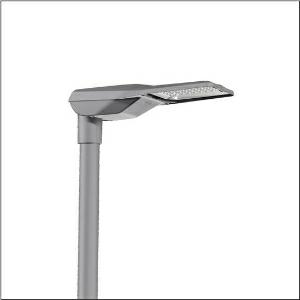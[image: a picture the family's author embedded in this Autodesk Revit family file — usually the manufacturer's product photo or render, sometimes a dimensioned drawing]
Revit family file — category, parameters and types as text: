
# Revit family: streetlight_sl_21_iq_mini___st0_8a_5xe2c21d08hb_7297
name_source: partatom
category: Lighting Fixtures
units: mm (PartAtom-declared; Revit-internal decimal feet)

## family parameters
Cut with Voids When Loaded = No
Host = Face
Light Source = No
Part Type = Normal
Room Calculation Point = No
Round Connector Dimension = Use Diameter
Shared = No

## types (1)
- --- (1 x LED, 7830 lm, 70.9 W, 2200K)
    Apparent Load = 71 VA
    CIE Flux Codes = 38 75 97 100 100
    Color Rendering = 70
    Color Temperature = 2200K
    Default Elevation = 1800 mm
    Description = Streetlight SL 21 iQ mini, mast luminaire, primary light control with lens, of PMMA, primary optical cover: cover, of toughened safety glass, transparent, light distribution: ST0.8a, light emission: direct distribution, primary light characteristic: asymmetric, installation type: post-top, side-entry, LED, High Power LED, rated luminous flux: 7.830lm, luminous efficacy: 110lm/W, light colour: 722, colour temperature: 2200K, control gear: iQ-Comfort, control: Auto-Match, Temp-Guard, Lumen-Switch, Night-Set, Smart-Wire, Light-Fading, Desk-Remote (wireless, voltage-free reading and setting of iQ features in the workshop via application-optimized NFC function/RFID function), optimised constant luminous flux control (CLO 2.0), pre-setting: linear dimming characteristic, mains connection: 220..240V, AC, 50/60Hz, start of lifetime: 71W, end of service life: 75W, reduction: 31W, luminaire housing, of diecast aluminium, powder-coated, Siteco® metallic grey (DB 702S), corrosivity category C5 mid according to DIN EN ISO 12944, please order mast flange separately, inclination adjustable: 0°, 5°, 10°, 15°, sealing non-destructively replaceable, multi-level sealing system, length: 628mm, width: 235mm, height: 110mm, mast flange for spigot size: 42mm (side-entry): 5XC10008XM4, 60/48mm (side-entry/post-top): 5XC10108XM2, 76/60mm (side-entry/post-top): 5XC10108XM1, mounting height: 4..8m, protection rating (complete): IP66, insulation class (complete): insulation class II (safety insulation), certification: CE, ENEC, ENEC+, VDE, impact resistance: IK10, permissible operating ambient temperature for outdoor applications: -40..+50°C, standard-compliant lighting for roads and squares, packaging unit: 1 piece

Light Distribution: ST0.8a
    Height = 110 mm
    Lamp = 1 x LED
    Lamp Light Flux = 7830 lm
    Lamp Power = 70.9 W
    Lamp count = 1
    Length = 625 mm
    Luminous efficacy = 110 lm/W
    Manufacturer = Siteco
    ModVariant = No
    Model = 5XE2C21D08HB
    Number of Poles = 1
    OnlyDefault = Yes
    Power Factor = 1
    Product Name = Streetlight SL 21 iQ mini | ST0.8a
    Product group = mast luminaire | pylon top
    ProductGroupID = 6100
    Protection Class = Protection class II
    Protection Degree = IP 66
    RLX_Detail_Level = 1
    RLX_Emergency_Light_Flux = 0 lm
    RLX_Emergency_Type = 0
    RLX_Emergency_Type_DB = No
    RlxData = <blob elided: 26309 chars, md5=c7411d6b>
    Socket = socket
    Standby Power = 0 W
    System Light Flux = 7830 lm
    System Power = 71 W
    Type Comments = factory setting: luminous flux: 100 % | dim-lin: 254 | 711 mA
    Type Image = l_1003519.jpg
    URL = http://relux.com
    VarID = @adj_179021
    Voltage = 0 V
    Weight = 0.00 kg
    Width = 234 mm

## geometry (parser evidence)
native form markers: Blend x4, Sweep x11
no freeform markers — native parametric forms only
